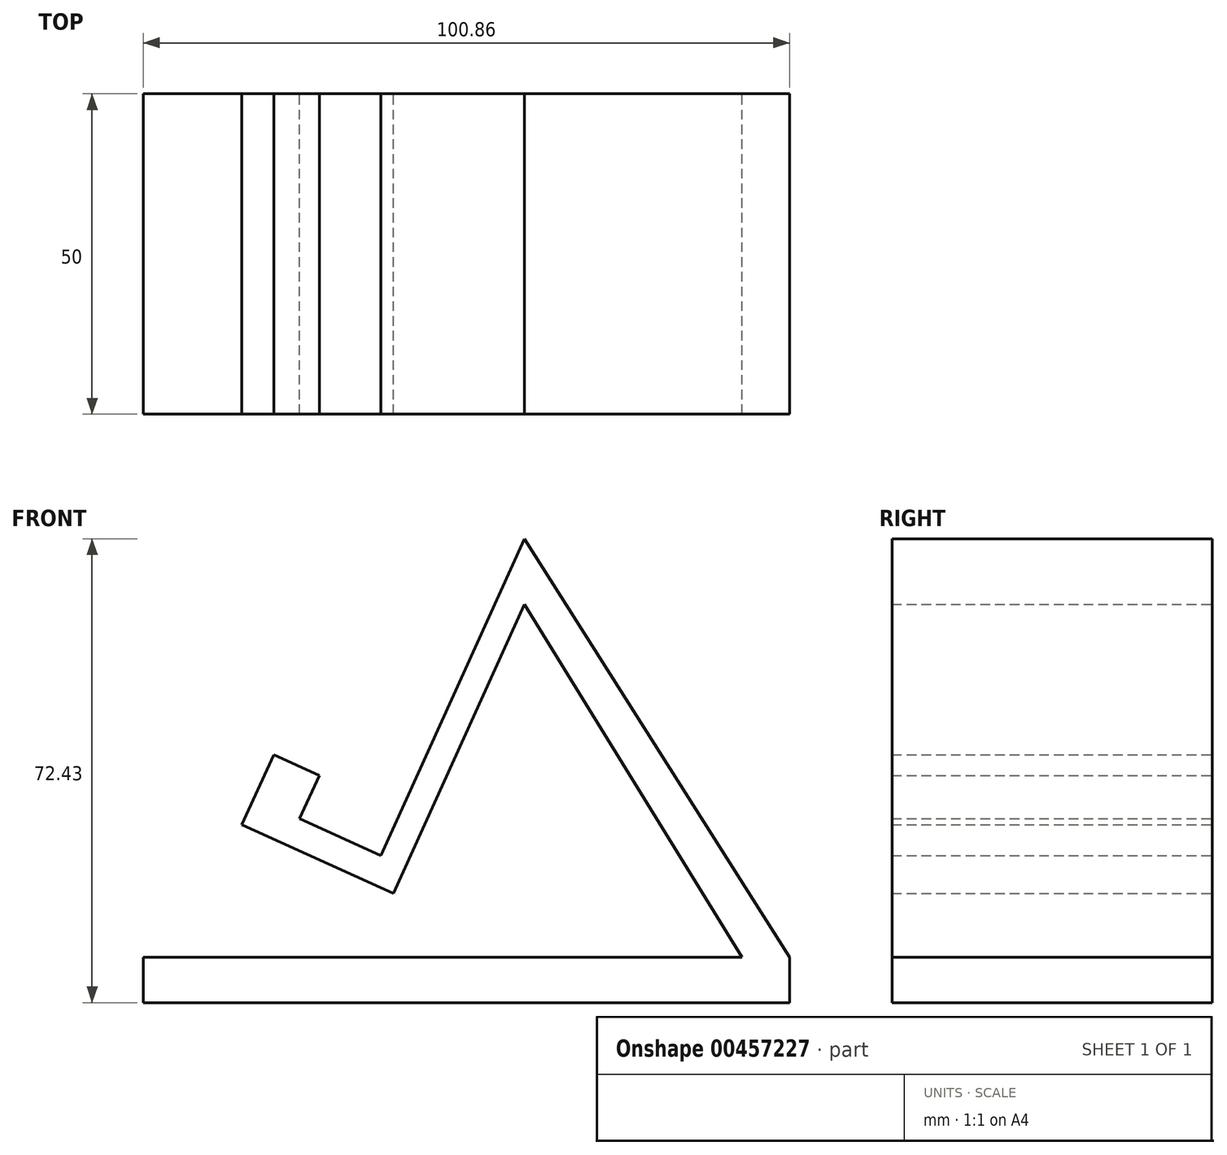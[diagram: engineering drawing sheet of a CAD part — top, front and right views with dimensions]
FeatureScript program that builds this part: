
annotation { "Feature Type Name" : "Feature", "Feature Type Description" : "" }
export const myFeature = defineFeature(function(context is Context, id is Id, definition is map)
    precondition{}
    {
        {
            var Q0;
            Q0=qCreatedBy(makeId("Front.planeOp"),FACE);
            var sketch = newSketch(context, id + "F0", { "sketchPlane" : qUnion([Q0])});
            skLineSegment(sketch, "E0", {"start": v(-51.41, 0) * mm, "end": v(49.45, 0) * mm});
            skLineSegment(sketch, "E1", {"start": v(49.45, 7.08) * mm, "end": v(49.45, 0) * mm});
            skLineSegment(sketch, "E2", {"start": v(49.45, 7.08) * mm, "end": v(8.06, 72.43) * mm});
            skLineSegment(sketch, "E3", {"start": v(8.06, 72.43) * mm, "end": v(-14.38, 22.98) * mm});
            skLineSegment(sketch, "E4", {"start": v(-14.38, 22.98) * mm, "end": v(-27.03, 28.72) * mm});
            skLineSegment(sketch, "E5", {"start": v(-27.03, 28.72) * mm, "end": v(-23.96, 35.5) * mm});
            skLineSegment(sketch, "E6", {"start": v(-23.96, 35.5) * mm, "end": v(-31.08, 38.73) * mm});
            skLineSegment(sketch, "E7", {"start": v(-31.08, 38.73) * mm, "end": v(-36.04, 27.8) * mm});
            skLineSegment(sketch, "E8", {"start": v(-36.04, 27.8) * mm, "end": v(-12.4, 17.07) * mm});
            skLineSegment(sketch, "E9", {"start": v(-12.4, 17.07) * mm, "end": v(8.06, 62.18) * mm});
            skLineSegment(sketch, "E10", {"start": v(8.06, 62.18) * mm, "end": v(42.04, 7.08) * mm});
            skLineSegment(sketch, "E11", {"start": v(42.04, 7.08) * mm, "end": v(-51.41, 7.08) * mm});
            skLineSegment(sketch, "E12", {"start": v(-51.41, 7.08) * mm, "end": v(-51.41, 0) * mm});
            skSolve(sketch);
        }
        {
            var Q0;
            Q0=makeQuery(id+"F0.imprint","IMPRINT",FACE,{"disambiguationData":[TD([[makeQuery(id+"F0.imprint","IMPRINT",EDGE,{"derivedFrom":sQuery(id+"F0.wireOp",EDGE,"E0")}),1.0]])]});
            extrude(context, id + "F1", {"entities" : qUnion([Q0]), "endBound" : BoundingType.SYMMETRIC, "depth" : 50 * mm});
        }
    });
